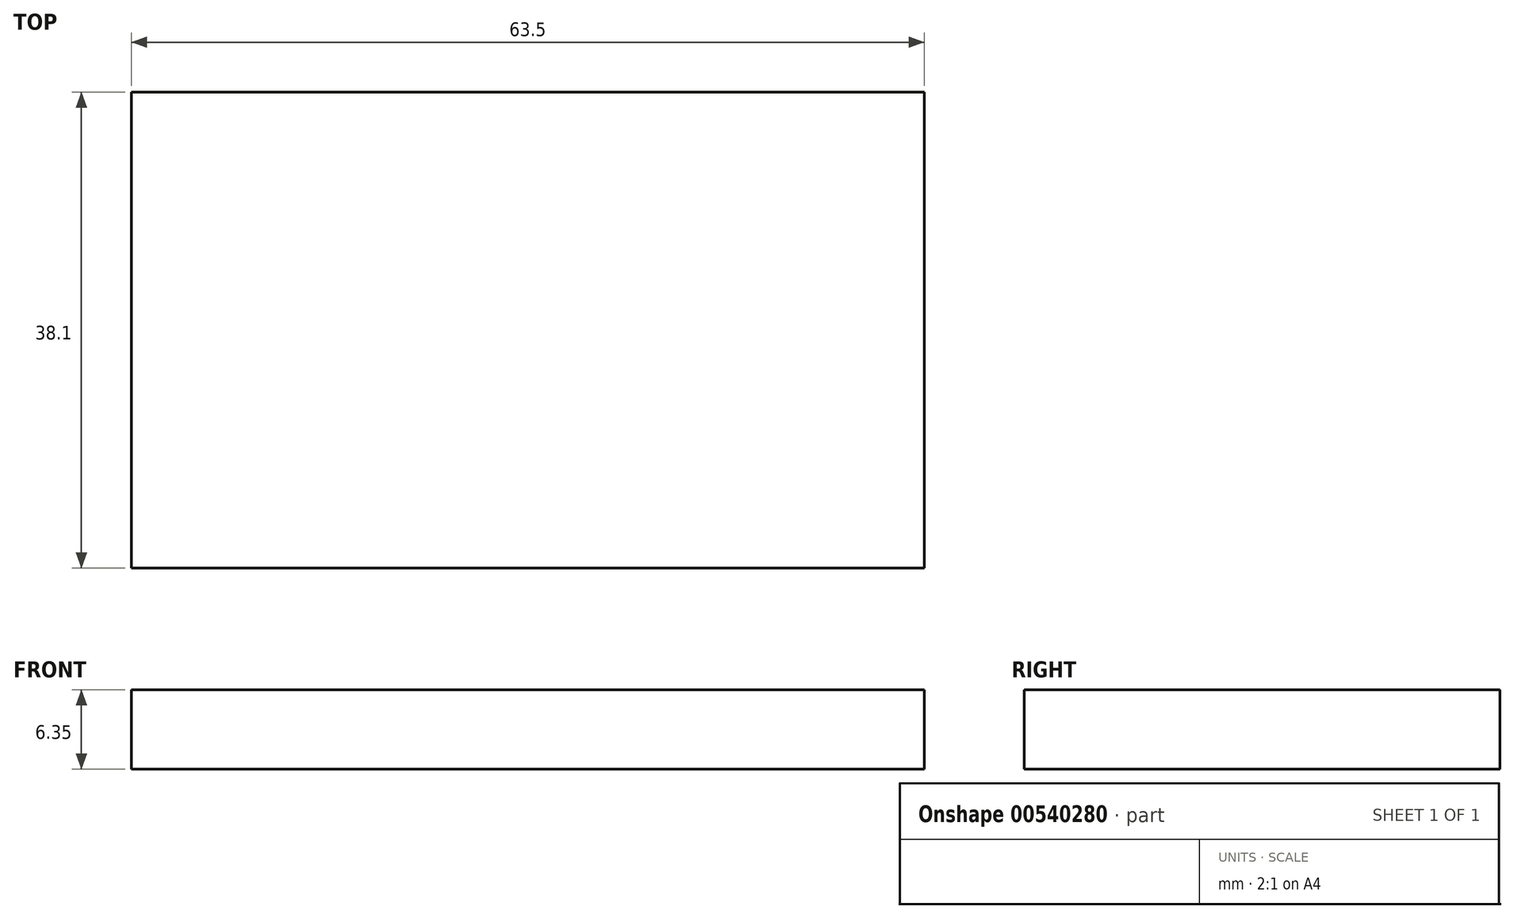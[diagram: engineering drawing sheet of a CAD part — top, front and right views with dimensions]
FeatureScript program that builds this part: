
annotation { "Feature Type Name" : "Feature", "Feature Type Description" : "" }
export const myFeature = defineFeature(function(context is Context, id is Id, definition is map)
    precondition{}
    {
        {
            var Q0;
            Q0=qCreatedBy(makeId("Top.planeOp"),FACE);
            var sketch = newSketch(context, id + "F0", { "sketchPlane" : qUnion([Q0])});
            skLineSegment(sketch, "E0", {"start": v(-87.74, 38.1) * mm, "end": v(-87.74, 0) * mm});
            skLineSegment(sketch, "E1", {"start": v(-87.74, 0) * mm, "end": v(-24.24, 0) * mm});
            skLineSegment(sketch, "E2", {"start": v(-24.24, 0) * mm, "end": v(-24.24, 38.1) * mm});
            skLineSegment(sketch, "E3", {"start": v(-24.24, 38.1) * mm, "end": v(-87.74, 38.1) * mm});
            skSolve(sketch);
        }
        {
            var Q0;
            Q0 = qSketchRegion(id + "F0", true);
            extrude(context, id + "F1", {"entities" : qUnion([Q0]), "depth" : 6.35 * mm, "offsetDistance" : 25.4 * mm});
        }
    });
